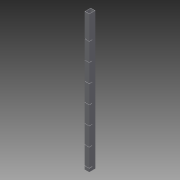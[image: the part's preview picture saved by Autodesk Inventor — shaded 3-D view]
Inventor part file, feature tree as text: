
AUTODESK INVENTOR PART (.ipt)
format: ipt  version: 2013 (Build 170138000, 138)  size: 139,264 bytes
history: native  units: in
note: dims shown in document units (in); Inventor stores cm internally (conversion verified against a paired STEP export)
features: other x4, extrude x1, sketch x1
ambient origin geometry x8: Origin, YZ Plane, XZ Plane, XY Plane, X Axis, Y Axis, Z Axis, Center Point
bodies: Solid1 (feature_tree)
feature tree (6):
  other  "Table"
  other  "squareTube1.5x2.ipt"
  extrude  "Extrusion2"  TaperAngle=0.0deg  [1 undecoded]
  other  "Solid1::squareTube1.5x2.ipt"
  other  "TaggingFeature1"
  sketch  "Sketch2"  dims[d0=1.5in d1=2.0in d2=0.125in d4=0.0in d20=2.7559in d22=6.0in d23=0.3937in d25=1.0in d27=1.0in d28=0.0in d29=0.1875in d30=1.0in]
note: 1 required parameter value undecoded (feature->parameter linkage not recoverable at this tier; creation-order binding heuristic only, values carry confidence <= 0.55)
